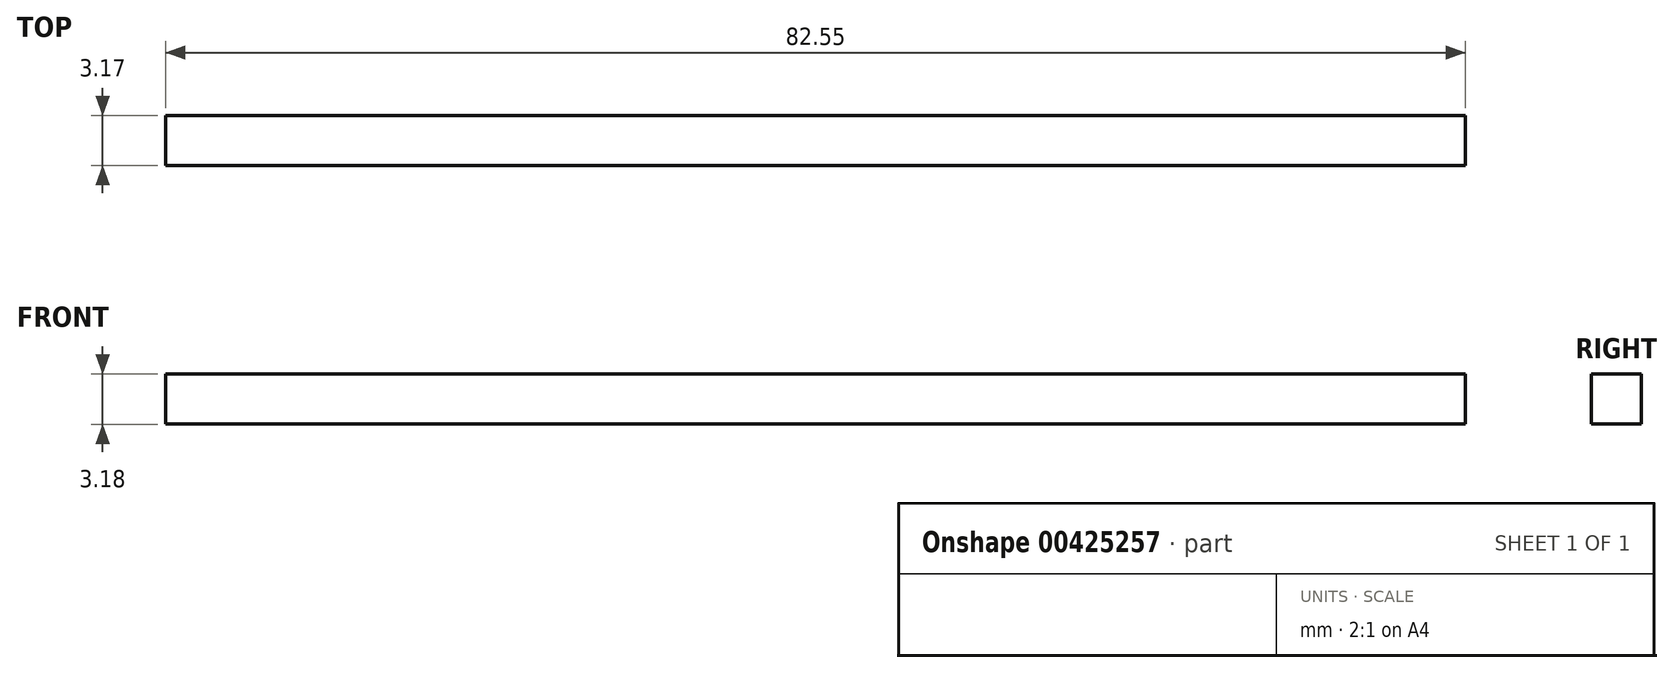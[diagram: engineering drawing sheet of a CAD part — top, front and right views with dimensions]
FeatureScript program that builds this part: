
annotation { "Feature Type Name" : "Feature", "Feature Type Description" : "" }
export const myFeature = defineFeature(function(context is Context, id is Id, definition is map)
    precondition{}
    {
        {
            var Q0;
            Q0=qCreatedBy(makeId("Front.planeOp"),FACE);
            var sketch = newSketch(context, id + "F0", { "sketchPlane" : qUnion([Q0])});
            skLineSegment(sketch, "E0.bottom", {"start": v(-32.03, 38.9) * mm, "end": v(50.52, 38.9) * mm});
            skLineSegment(sketch, "E0.top", {"start": v(-32.03, 35.73) * mm, "end": v(50.52, 35.73) * mm});
            skLineSegment(sketch, "E0.left", {"start": v(-32.03, 38.9) * mm, "end": v(-32.03, 35.73) * mm});
            skLineSegment(sketch, "E0.right", {"start": v(50.52, 38.9) * mm, "end": v(50.52, 35.73) * mm});
            skSolve(sketch);
        }
        {
            var Q0;
            Q0 = qSketchRegion(id + "F0", true);
            extrude(context, id + "F1", {"entities" : qUnion([Q0]), "depth" : 3.17 * mm});
        }
    });
